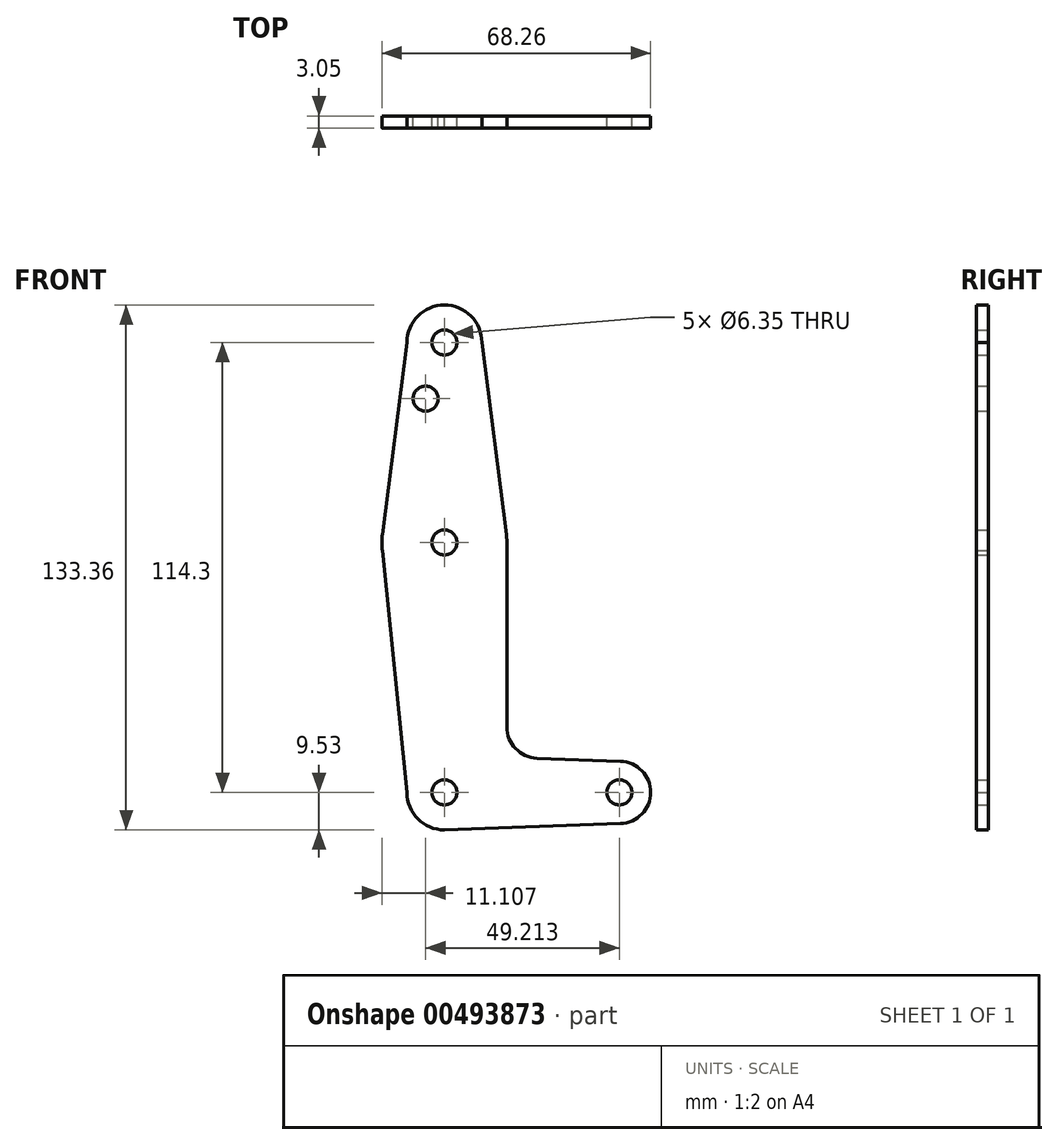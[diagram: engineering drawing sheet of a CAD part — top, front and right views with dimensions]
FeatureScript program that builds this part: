
annotation { "Feature Type Name" : "Feature", "Feature Type Description" : "" }
export const myFeature = defineFeature(function(context is Context, id is Id, definition is map)
    precondition{}
    {
        {
            var Q0;
            Q0=qCreatedBy(makeId("Front.planeOp"),FACE);
            var sketch = newSketch(context, id + "F0", { "sketchPlane" : qUnion([Q0])});
            skLineSegment(sketch, "E0", {"start": v(0, 0) * mm, "end": v(0, 114.3) * mm, "construction": true});
            skLineSegment(sketch, "E1", {"start": v(0, 0) * mm, "end": v(44.45, 0) * mm, "construction": true});
            skCircle(sketch, "E2", {"center": v(0, 114.3) * mm, "radius": 9.53 * mm});
            skCircle(sketch, "E3", {"center": v(0, 63.5) * mm, "radius": 15.88 * mm});
            skCircle(sketch, "E4", {"center": v(0, 0) * mm, "radius": 9.53 * mm});
            skCircle(sketch, "E5", {"center": v(44.45, 0) * mm, "radius": 7.94 * mm});
            skLineSegment(sketch, "E6", {"start": v(-9.53, 114.3) * mm, "end": v(-15.75, 65.5) * mm});
            skLineSegment(sketch, "E7", {"start": v(9.53, 114.3) * mm, "end": v(15.75, 65.5) * mm});
            skLineSegment(sketch, "E8", {"start": v(-15.75, 61.5) * mm, "end": v(-9.53, 0) * mm});
            skLineSegment(sketch, "E9", {"start": v(15.87, 63.5) * mm, "end": v(15.88, 16.63) * mm});
            skLineSegment(sketch, "E10", {"start": v(23.54, 8.69) * mm, "end": v(44.73, 7.93) * mm});
            skLineSegment(sketch, "E11", {"start": v(0, -9.53) * mm, "end": v(44.73, -7.93) * mm});
            skCircle(sketch, "E12", {"center": v(0, 114.3) * mm, "radius": 3.18 * mm});
            skCircle(sketch, "E13", {"center": v(0, 63.5) * mm, "radius": 3.18 * mm});
            skCircle(sketch, "E14", {"center": v(0, 0) * mm, "radius": 3.18 * mm});
            skCircle(sketch, "E15", {"center": v(44.45, 0) * mm, "radius": 3.18 * mm});
            skCircle(sketch, "E16", {"center": v(-4.76, 100.03) * mm, "radius": 3.18 * mm});
            skArc(sketch, "E17.filletArc", {"start": v(15.88, 16.63) * mm, "mid": v(18.1, 11.11) * mm, "end": v(23.54, 8.69) * mm});
            skSolve(sketch);
        }
        {
            var Q0;
            {var subQ1=sQuery(id+"F0.wireOp",EDGE,"E6");Q0=makeQuery(id+"F0.imprint","IMPRINT",FACE,{"disambiguationData":[TD([[makeQuery(id+"F0.imprint","IMPRINT",EDGE,{"derivedFrom":subQ1}),1.0]])]});}
            var Q1;
            Q1=makeQuery(id+"F0.imprint","IMPRINT",FACE,{"disambiguationData":[TD([[makeQuery(id+"F0.imprint","IMPRINT",EDGE,{"derivedFrom":sQuery(id+"F0.wireOp",EDGE,"E13")}),-1.0]])]});
            var Q2;
            Q2=makeQuery(id+"F0.imprint","IMPRINT",FACE,{"disambiguationData":[TD([[makeQuery(id+"F0.imprint","IMPRINT",EDGE,{"derivedFrom":sQuery(id+"F0.wireOp",EDGE,"E12")}),-1.0]])]});
            var Q3;
            {var subQ4=sQuery(id+"F0.wireOp",EDGE,"E8");Q3=makeQuery(id+"F0.imprint","IMPRINT",FACE,{"disambiguationData":[TD([[makeQuery(id+"F0.imprint","IMPRINT",EDGE,{"derivedFrom":subQ4}),1.0]])]});}
            var Q4;
            Q4=makeQuery(id+"F0.imprint","IMPRINT",FACE,{"disambiguationData":[TD([[makeQuery(id+"F0.imprint","IMPRINT",EDGE,{"derivedFrom":sQuery(id+"F0.wireOp",EDGE,"E14")}),-1.0]])]});
            var Q5;
            Q5=makeQuery(id+"F0.imprint","IMPRINT",FACE,{"disambiguationData":[TD([[makeQuery(id+"F0.imprint","IMPRINT",EDGE,{"derivedFrom":sQuery(id+"F0.wireOp",EDGE,"E15")}),-1.0]])]});
            extrude(context, id + "F1", {"entities" : qUnion([Q0, Q1, Q2, Q3, Q4, Q5]), "depth" : 3.05 * mm});
        }
    });
